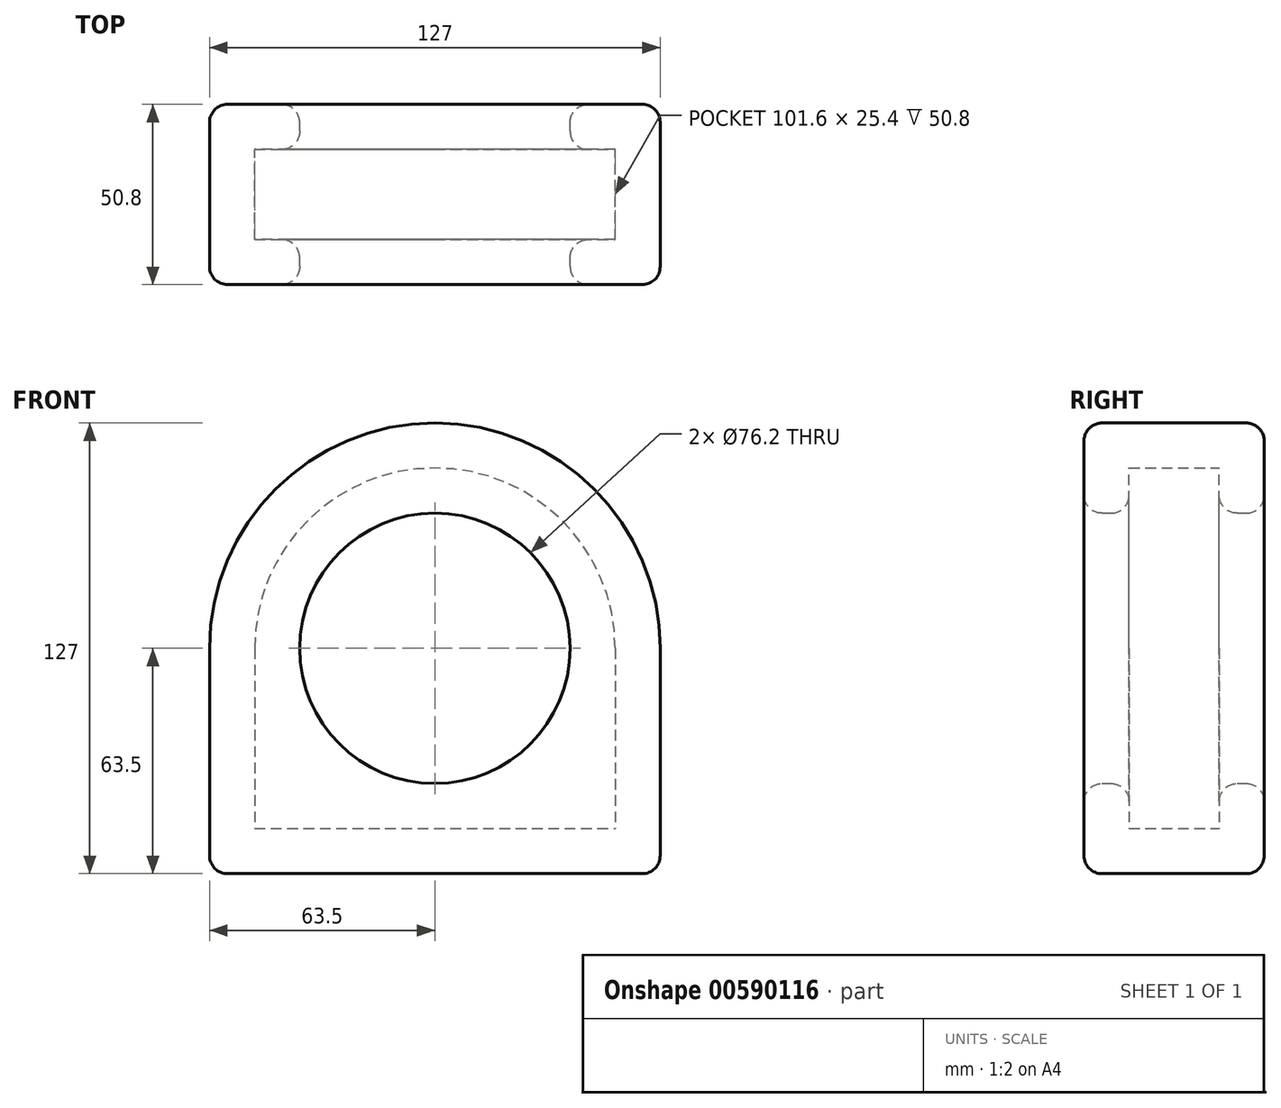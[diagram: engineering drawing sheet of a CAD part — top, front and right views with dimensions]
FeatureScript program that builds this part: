
annotation { "Feature Type Name" : "Feature", "Feature Type Description" : "" }
export const myFeature = defineFeature(function(context is Context, id is Id, definition is map)
    precondition{}
    {
        {
            var Q0;
            Q0=qCreatedBy(makeId("Front.planeOp"),FACE);
            var sketch = newSketch(context, id + "F0", { "sketchPlane" : qUnion([Q0])});
            skCircle(sketch, "E0", {"center": v(0, 0) * mm, "radius": 63.5 * mm});
            skCircle(sketch, "E1", {"center": v(0, 0) * mm, "radius": 38.1 * mm});
            skLineSegment(sketch, "E2", {"start": v(-63.5, 0) * mm, "end": v(-63.5, -63.5) * mm});
            skLineSegment(sketch, "E3", {"start": v(-63.5, -63.5) * mm, "end": v(0, -63.5) * mm});
            skLineSegment(sketch, "E4", {"start": v(63.5, 0) * mm, "end": v(63.5, -63.5) * mm});
            skLineSegment(sketch, "E5", {"start": v(63.5, -63.5) * mm, "end": v(0, -63.5) * mm});
            skSolve(sketch);
        }
        {
            var Q0;
            Q0=makeQuery(id+"F0.imprint","IMPRINT",FACE,{"disambiguationData":[TD([[makeQuery(id+"F0.imprint","IMPRINT",EDGE,{"derivedFrom":sQuery(id+"F0.wireOp",EDGE,"E1")}),-1.0]])]});
            var Q1;
            {var subQ0=sQuery(id+"F0.wireOp",EDGE,"E2");Q1=makeQuery(id+"F0.imprint","IMPRINT",FACE,{"disambiguationData":[TD([[makeQuery(id+"F0.imprint","IMPRINT",EDGE,{"derivedFrom":subQ0}),1.0]])]});}
            var Q2;
            {var subQ0=sQuery(id+"F0.wireOp",EDGE,"E4");Q2=makeQuery(id+"F0.imprint","IMPRINT",FACE,{"disambiguationData":[TD([[makeQuery(id+"F0.imprint","IMPRINT",EDGE,{"derivedFrom":subQ0}),-1.0]])]});}
            extrude(context, id + "F1", {"entities" : qUnion([Q0, Q1, Q2]), "depth" : 25.4 * mm, "offsetDistance" : 25.4 * mm, "hasSecondDirection" : true, "secondDirectionOppositeDirection" : true, "secondDirectionDepth" : 25.4 * mm});
        }
        {
            var Q0;
            Q0=makeQuery(id+"F1.opExtrude","SWEPT_FACE",FACE,{"disambiguationData":[OSD([sQuery(id+"F0.wireOp",EDGE,"E1")])]});
            shell(context, id + "F2", {"entities" : qUnion([Q0]), "thickness" : 12.7 * mm});
        }
        {
            var Q0;
            Q0=makeQuery(id+"F1.opExtrude","CAP_FACE",FACE,{"disambiguationData":[OSD([sQuery(id+"F0.wireOp",EDGE,"E0"),sQuery(id+"F0.wireOp",EDGE,"E1"),sQuery(id+"F0.wireOp",EDGE,"E2"),sQuery(id+"F0.wireOp",EDGE,"E3"),sQuery(id+"F0.wireOp",EDGE,"E4"),sQuery(id+"F0.wireOp",EDGE,"E5")])],"isStart":false});
            var Q1;
            Q1=makeQuery(id+"F1.opExtrude","CAP_EDGE",EDGE,{"disambiguationData":[OSD([sQuery(id+"F0.wireOp",EDGE,"E1")])],"isStart":false});
            var Q2;
            Q2=makeQuery(id+"F1.opExtrude","CAP_EDGE",EDGE,{"disambiguationData":[OSD([sQuery(id+"F0.wireOp",EDGE,"E0")])],"isStart":true});
            var Q3;
            Q3=makeQuery(id+"F1.opExtrude","CAP_EDGE",EDGE,{"disambiguationData":[OSD([sQuery(id+"F0.wireOp",EDGE,"E1")])],"isStart":true});
            var Q4;
            {var subQ0=sQuery(id+"F0.wireOp",EDGE,"E1");Q4=makeQuery(id+"F2.opShell","OFFSET_EDGE",EDGE,{"disambiguationData":[OSD([subQ0]),TDD([makeQuery(id+"F1.opExtrude","CAP_EDGE",EDGE,{"disambiguationData":[OSD([subQ0])],"isStart":true})])]});}
            var Q5;
            {var subQ0=sQuery(id+"F0.wireOp",EDGE,"E1");Q5=makeQuery(id+"F2.opShell","OFFSET_EDGE",EDGE,{"disambiguationData":[OSD([subQ0]),TDD([makeQuery(id+"F1.opExtrude","CAP_EDGE",EDGE,{"disambiguationData":[OSD([subQ0])],"isStart":false})])]});}
            var Q6;
            Q6=makeQuery(id+"F1.opExtrude","SWEPT_EDGE",EDGE,{"disambiguationData":[OSD([sQuery(id+"F0.wireOp",EDGE,"E2"),sQuery(id+"F0.wireOp",EDGE,"E3")])]});
            var Q7;
            Q7=makeQuery(id+"F1.opExtrude","CAP_EDGE",EDGE,{"disambiguationData":[OSD([sQuery(id+"F0.wireOp",EDGE,"E3"),sQuery(id+"F0.wireOp",EDGE,"E5")])],"isStart":true});
            var Q8;
            Q8=makeQuery(id+"F1.opExtrude","SWEPT_EDGE",EDGE,{"disambiguationData":[OSD([sQuery(id+"F0.wireOp",EDGE,"E4"),sQuery(id+"F0.wireOp",EDGE,"E5")])]});
            fillet(context, id + "F3", {"entities" : qUnion([Q0, Q1, Q2, Q3, Q4, Q5, Q6, Q7, Q8]), "radius" : 5.08 * mm, "tangentPropagation" : true, "allowEdgeOverflow" : false});
        }
    });
